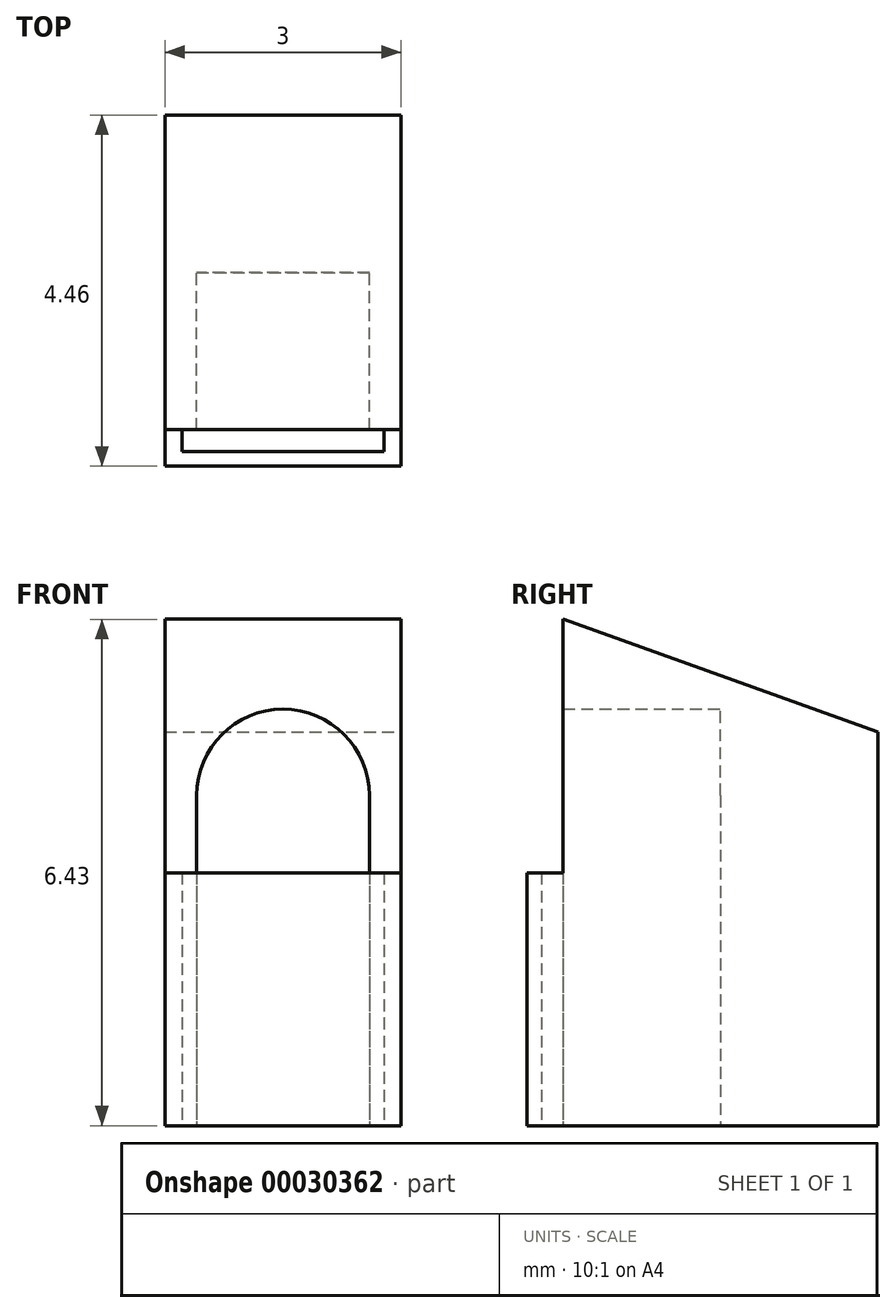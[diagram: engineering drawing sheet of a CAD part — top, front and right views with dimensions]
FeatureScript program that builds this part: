
annotation { "Feature Type Name" : "Feature", "Feature Type Description" : "" }
export const myFeature = defineFeature(function(context is Context, id is Id, definition is map)
    precondition{}
    {
        {
            var Q0;
            Q0=qCreatedBy(makeId("Top.planeOp"),FACE);
            var sketch = newSketch(context, id + "F0", { "sketchPlane" : qUnion([Q0])});
            skLineSegment(sketch, "E0.rect.bottom", {"start": v(-1.5, 2) * mm, "end": v(1.5, 2) * mm});
            skLineSegment(sketch, "E0.rect.top", {"start": v(-1.5, -2) * mm, "end": v(1.5, -2) * mm});
            skLineSegment(sketch, "E0.rect.left", {"start": v(-1.5, 2) * mm, "end": v(-1.5, -2) * mm});
            skLineSegment(sketch, "E0.rect.right", {"start": v(1.5, 2) * mm, "end": v(1.5, -2) * mm});
            skPoint(sketch, "E0.rect.middle", {"position": v(0, 0) * mm});
            skLineSegment(sketch, "E1.top", {"start": v(-1.5, -2.46) * mm, "end": v(1.5, -2.46) * mm});
            skLineSegment(sketch, "E1.left", {"start": v(-1.5, -2) * mm, "end": v(-1.5, -2.46) * mm});
            skLineSegment(sketch, "E1.right", {"start": v(1.5, -2) * mm, "end": v(1.5, -2.46) * mm});
            skLineSegment(sketch, "E2.bottom", {"start": v(-1.28, -2) * mm, "end": v(1.28, -2) * mm});
            skLineSegment(sketch, "E2.top", {"start": v(-1.28, -2.28) * mm, "end": v(1.28, -2.28) * mm});
            skLineSegment(sketch, "E2.left", {"start": v(-1.28, -2) * mm, "end": v(-1.28, -2.28) * mm});
            skLineSegment(sketch, "E2.right", {"start": v(1.28, -2) * mm, "end": v(1.28, -2.28) * mm});
            skPoint(sketch, "E3", {"position": v(0, -2.28) * mm});
            skPoint(sketch, "E4", {"position": v(0, -2.46) * mm});
            skSolve(sketch);
        }
        {
            var Q0;
            Q0=makeQuery(id+"F0.imprint","IMPRINT",FACE,{"disambiguationData":[TD([[makeQuery(id+"F0.imprint","IMPRINT",EDGE,{"derivedFrom":sQuery(id+"F0.wireOp",EDGE,"E0.rect.bottom")}),-1.0]])]});
            extrude(context, id + "F1", {"entities" : qUnion([Q0]), "depth" : 5 * mm});
        }
        {
            var Q0;
            Q0=qCreatedBy(makeId("Right.planeOp"),FACE);
            var sketch = newSketch(context, id + "F2", { "sketchPlane" : qUnion([Q0])});
            skLineSegment(sketch, "E5", {"start": v(2, 5) * mm, "end": v(2, 5) * mm});
            skLineSegment(sketch, "E6", {"start": v(2, 5) * mm, "end": v(-2, 6.43) * mm});
            skLineSegment(sketch, "E7", {"start": v(-2, 6.43) * mm, "end": v(-2, 5) * mm});
            skLineSegment(sketch, "E8", {"start": v(-2, 5) * mm, "end": v(2, 5) * mm});
            skSolve(sketch);
        }
        {
            var Q0;
            {var subQ2=sQuery(id+"F2.wireOp",EDGE,"E6");Q0=makeQuery(id+"F2.imprint","IMPRINT",FACE,{"disambiguationData":[TD([[makeQuery(id+"F2.imprint","IMPRINT",EDGE,{"derivedFrom":subQ2}),1.0]])]});}
            var Q1;
            Q1=makeQuery(id+"F1.opExtrude","SWEPT_FACE",FACE,{"disambiguationData":[OSD([sQuery(id+"F0.wireOp",EDGE,"E0.rect.right")])]});
            var Q2;
            Q2=makeQuery(id+"F1.opExtrude","SWEPT_FACE",FACE,{"disambiguationData":[OSD([sQuery(id+"F0.wireOp",EDGE,"E0.rect.left")])]});
            extrude(context, id + "F3", {"entities" : qUnion([Q0]), "operationType" : NewBodyOperationType.ADD, "endBound" : BoundingType.UP_TO_SURFACE, "endBoundEntityFace" : qUnion([Q1]), "depth" : 25 * mm, "hasSecondDirection" : true, "secondDirectionBound" : SecondDirectionBoundingType.UP_TO_SURFACE, "secondDirectionOppositeDirection" : true, "secondDirectionBoundEntityFace" : qUnion([Q2]), "secondDirectionDepth" : 25 * mm});
        }
        {
            var Q0;
            Q0=qCreatedBy(makeId("Front.planeOp"),FACE);
            var sketch = newSketch(context, id + "F4", { "sketchPlane" : qUnion([Q0])});
            skArc(sketch, "E9", {"start": v(1.1, 4.2) * mm, "mid": v(0, 5.3) * mm, "end": v(-1.1, 4.2) * mm});
            skLineSegment(sketch, "E10.top", {"start": v(-1.1, 0) * mm, "end": v(1.1, 0) * mm});
            skLineSegment(sketch, "E10.left", {"start": v(-1.1, 4.2) * mm, "end": v(-1.1, 0) * mm});
            skLineSegment(sketch, "E10.right", {"start": v(1.1, 4.2) * mm, "end": v(1.1, 0) * mm});
            skSolve(sketch);
        }
        {
            var Q0;
            Q0=makeQuery(id+"F4.imprint","IMPRINT",FACE,{"disambiguationData":[TD([[makeQuery(id+"F4.imprint","IMPRINT",EDGE,{"derivedFrom":sQuery(id+"F4.wireOp",EDGE,"E9")}),1.0]])]});
            extrude(context, id + "F5", {"entities" : qUnion([Q0]), "operationType" : NewBodyOperationType.REMOVE, "depth" : 6.23 * mm});
        }
        {
            var Q0;
            Q0=makeQuery(id+"F0.imprint","IMPRINT",FACE,{"disambiguationData":[TD([[makeQuery(id+"F0.imprint","IMPRINT",EDGE,{"derivedFrom":sQuery(id+"F0.wireOp",EDGE,"E1.top")}),1.0]])]});
            extrude(context, id + "F6", {"entities" : qUnion([Q0]), "operationType" : NewBodyOperationType.ADD, "depth" : 3.2 * mm});
        }
    });
